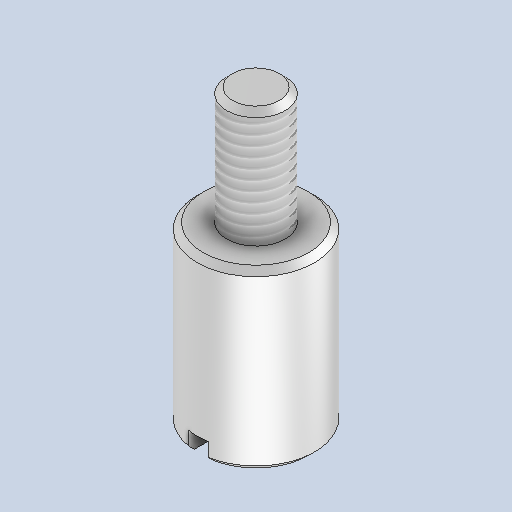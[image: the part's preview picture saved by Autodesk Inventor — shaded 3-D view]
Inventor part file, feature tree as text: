
AUTODESK INVENTOR PART (.ipt)
format: ipt  version: 2024.2 (Build 282272000, 272)  size: 313,856 bytes
history: native  units: mm
features: sketch x2, revolve x1, extrude x1, hole x1, thread x1, chamfer x1
ambient origin geometry x8: Origin, YZ Plane, XZ Plane, XY Plane, X Axis, Y Axis, Z Axis, Center Point
bodies: Solid1 (feature_tree)
feature tree (7):
  revolve  "Revolution1"  [1 undecoded]
  sketch  "Sketch2"  dims[d3=3.0mm d4=6.0mm d5=90.0deg d6=1.0mm d7=1.0mm d8=0.0mm d9=2.459mm d10=6.0mm d11=4.0mm d12=2.0mm d13=90.0deg d14=6.0mm d15=0.0mm d16=6.0mm d17=0.0mm d18=0.3mm d19=2.0mm d20=45.0deg]
  extrude  "Extrusion1"  Depth=3.0mm
  hole  "Hole1"  [1 undecoded]
  thread  "Thread1"  [1 undecoded]
  chamfer  "Chamfer1"  Distance=1.0mm
  sketch  "Sketch1"  dims[d1=6.0mm d2=9.0mm]
note: 3 required parameter values undecoded (feature->parameter linkage not recoverable at this tier; creation-order binding heuristic only, values carry confidence <= 0.55)